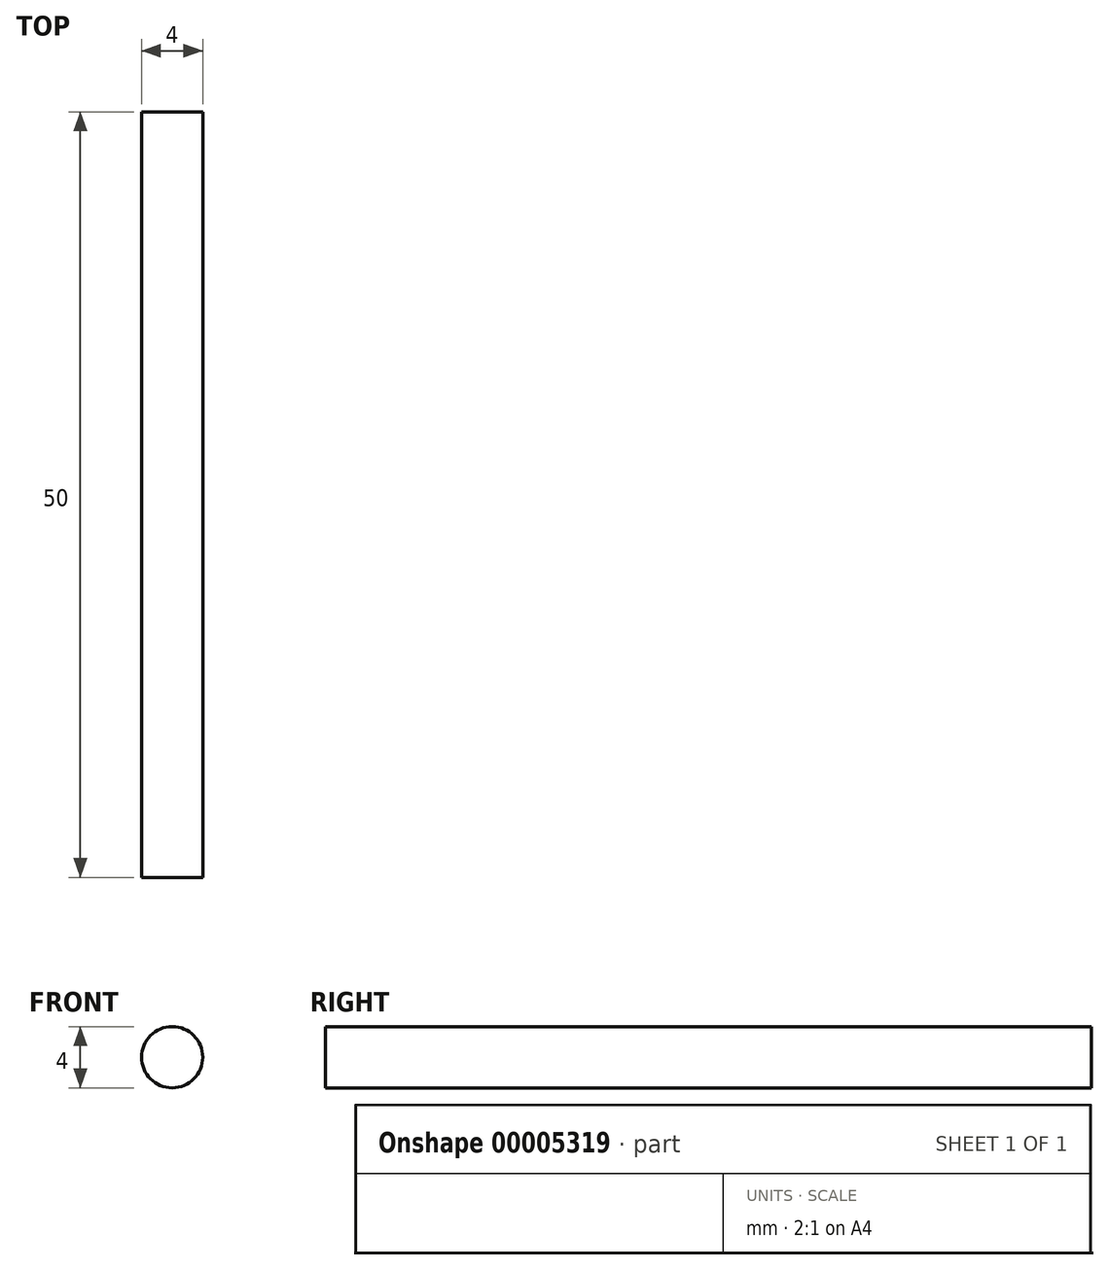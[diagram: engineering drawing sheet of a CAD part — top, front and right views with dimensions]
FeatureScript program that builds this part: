
annotation { "Feature Type Name" : "Feature", "Feature Type Description" : "" }
export const myFeature = defineFeature(function(context is Context, id is Id, definition is map)
    precondition{}
    {
        {
            var Q0;
            Q0=qCreatedBy(makeId("Front.planeOp"),FACE);
            var sketch = newSketch(context, id + "F0", { "sketchPlane" : qUnion([Q0])});
            skCircle(sketch, "E0", {"center": v(0, 0) * mm, "radius": 2 * mm});
            skSolve(sketch);
        }
        {
            var Q0;
            Q0=makeQuery(id+"F0.imprint","IMPRINT",FACE,{"disambiguationData":[TD([[makeQuery(id+"F0.imprint","IMPRINT",EDGE,{"derivedFrom":sQuery(id+"F0.wireOp",EDGE,"E0")}),1.0]])]});
            extrude(context, id + "F1", {"entities" : qUnion([Q0]), "depth" : 50 * mm});
        }
    });
